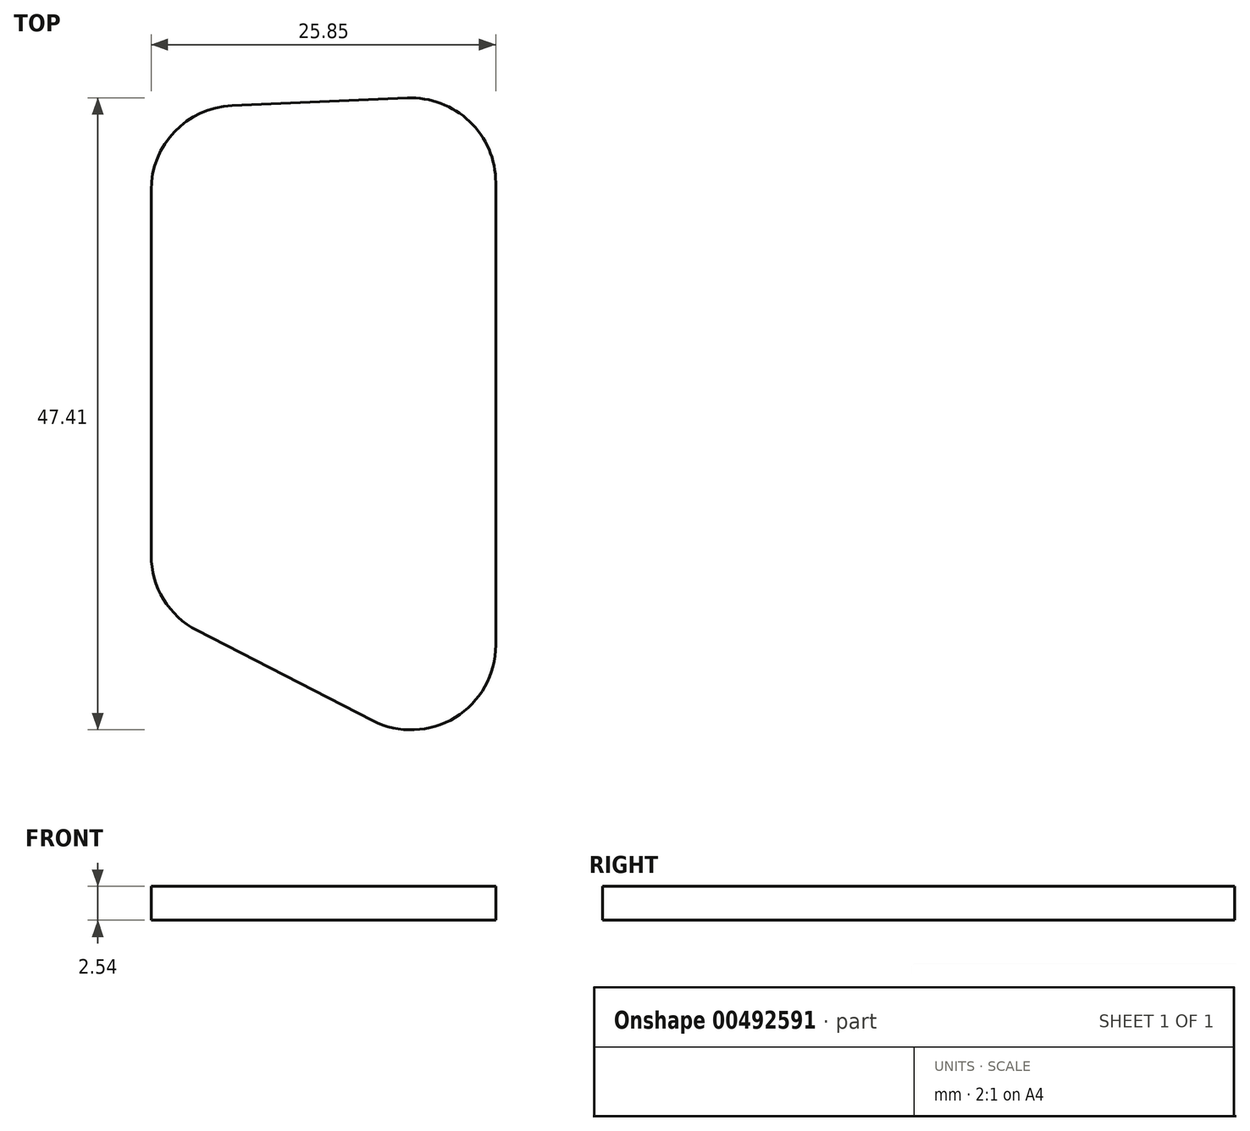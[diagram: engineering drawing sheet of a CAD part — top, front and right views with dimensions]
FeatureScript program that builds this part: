
annotation { "Feature Type Name" : "Feature", "Feature Type Description" : "" }
export const myFeature = defineFeature(function(context is Context, id is Id, definition is map)
    precondition{}
    {
        {
            var Q0;
            Q0=qCreatedBy(makeId("Top.planeOp"),FACE);
            var sketch = newSketch(context, id + "F0", { "sketchPlane" : qUnion([Q0])});
            skLineSegment(sketch, "E0", {"start": v(-9.25, -50.23) * mm, "end": v(-22.4, -43.47) * mm});
            skLineSegment(sketch, "E1", {"start": v(-25.85, -37.83) * mm, "end": v(-25.85, -10.44) * mm});
            skLineSegment(sketch, "E2", {"start": v(-19.77, -4.1) * mm, "end": v(-6.63, -3.53) * mm});
            skLineSegment(sketch, "E3", {"start": v(0, -9.87) * mm, "end": v(0, -44.58) * mm});
            skPoint(sketch, "E4.visualSharp", {"position": v(-25.85, -41.7) * mm});
            skArc(sketch, "E4.filletArc", {"start": v(-25.85, -37.83) * mm, "mid": v(-24.92, -41.13) * mm, "end": v(-22.4, -43.47) * mm});
            skPoint(sketch, "E5.visualSharp", {"position": v(-25.85, -4.37) * mm});
            skArc(sketch, "E5.filletArc", {"start": v(-19.77, -4.1) * mm, "mid": v(-24.08, -6.05) * mm, "end": v(-25.85, -10.44) * mm});
            skPoint(sketch, "E6.visualSharp", {"position": v(0, -3.24) * mm});
            skArc(sketch, "E6.filletArc", {"start": v(0, -9.87) * mm, "mid": v(-1.96, -5.28) * mm, "end": v(-6.63, -3.53) * mm});
            skPoint(sketch, "E7.visualSharp", {"position": v(0, -54.99) * mm});
            skArc(sketch, "E7.filletArc", {"start": v(-9.25, -50.23) * mm, "mid": v(-3.04, -50) * mm, "end": v(0, -44.58) * mm});
            skSolve(sketch);
        }
        {
            var Q0;
            Q0=makeQuery(id+"F0.imprint","IMPRINT",FACE,{"disambiguationData":[TD([[makeQuery(id+"F0.imprint","IMPRINT",EDGE,{"derivedFrom":sQuery(id+"F0.wireOp",EDGE,"E0")}),-1.0]])]});
            extrude(context, id + "F1", {"entities" : qUnion([Q0]), "depth" : 2.54 * mm});
        }
    });
